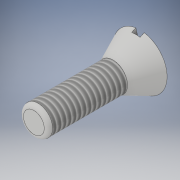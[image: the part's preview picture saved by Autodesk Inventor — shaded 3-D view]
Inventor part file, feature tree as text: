
AUTODESK INVENTOR PART (.ipt)
format: ipt  version: 2019 (Build 230136000, 136)  size: 138,240 bytes
history: native  units: mm
features: sketch x2, revolve x1, plane x1, extrude x1, thread x1, fillet x1
ambient origin geometry x8: Origin, YZ Plane, XZ Plane, XY Plane, X Axis, Y Axis, Z Axis, Center Point
bodies: Solid1 (feature_tree)
feature tree (7):
  revolve  "Revolution1"  [1 undecoded]
  plane  "Work Plane1"
  extrude  "Extrusion1"  Depth=0.75mm
  thread  "Thread1"  [1 undecoded]
  fillet  "Fillet1"  [1 undecoded]
  sketch  "Sketch1"  dims[d0=13.5mm d1=1.75mm]
  sketch  "Sketch2"  dims[d2=3.25mm d4=0.75mm d5=9.5mm d6=90.0deg d7=-13.5mm d8=1.0mm d9=0.5mm d10=1.25mm d11=0.0mm d12=10.0mm d13=0.0mm d14=0.5mm]
note: 3 required parameter values undecoded (feature->parameter linkage not recoverable at this tier; creation-order binding heuristic only, values carry confidence <= 0.55)